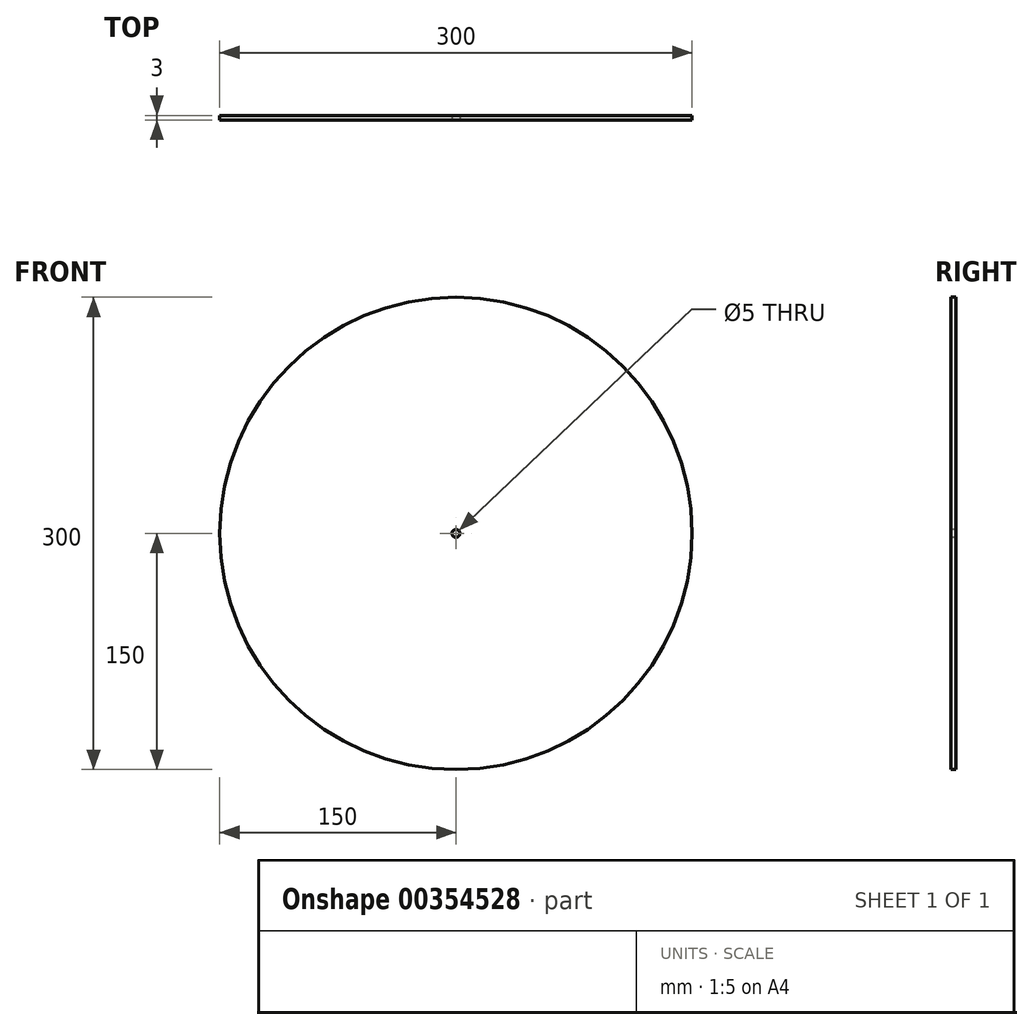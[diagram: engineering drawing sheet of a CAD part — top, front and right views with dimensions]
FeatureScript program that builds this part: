
annotation { "Feature Type Name" : "Feature", "Feature Type Description" : "" }
export const myFeature = defineFeature(function(context is Context, id is Id, definition is map)
    precondition{}
    {
        {
            var Q0;
            Q0=qCreatedBy(makeId("Front.planeOp"),FACE);
            var sketch = newSketch(context, id + "F0", { "sketchPlane" : qUnion([Q0])});
            skCircle(sketch, "E0", {"center": v(0, 0) * mm, "radius": 150 * mm});
            skSolve(sketch);
        }
        {
            var Q0;
            Q0 = qSketchRegion(id + "F0", true);
            extrude(context, id + "F1", {"entities" : qUnion([Q0]), "depth" : 3 * mm});
        }
        {
            var Q0;
            Q0=makeQuery(id+"F1.opExtrude","CAP_FACE",FACE,{"disambiguationData":[OSD([sQuery(id+"F0.wireOp",EDGE,"E0")])],"isStart":false});
            var sketch = newSketch(context, id + "F2", { "sketchPlane" : qUnion([Q0])});
            skCircle(sketch, "E1", {"center": v(0, 0) * mm, "radius": 2.5 * mm});
            skSolve(sketch);
        }
        {
            var Q0;
            Q0 = qSketchRegion(id + "F2", true);
            extrude(context, id + "F3", {"entities" : qUnion([Q0]), "operationType" : NewBodyOperationType.REMOVE, "endBound" : BoundingType.UP_TO_NEXT, "oppositeDirection" : true, "depth" : 25 * mm, "offsetDistance" : 25 * mm});
        }
    });
